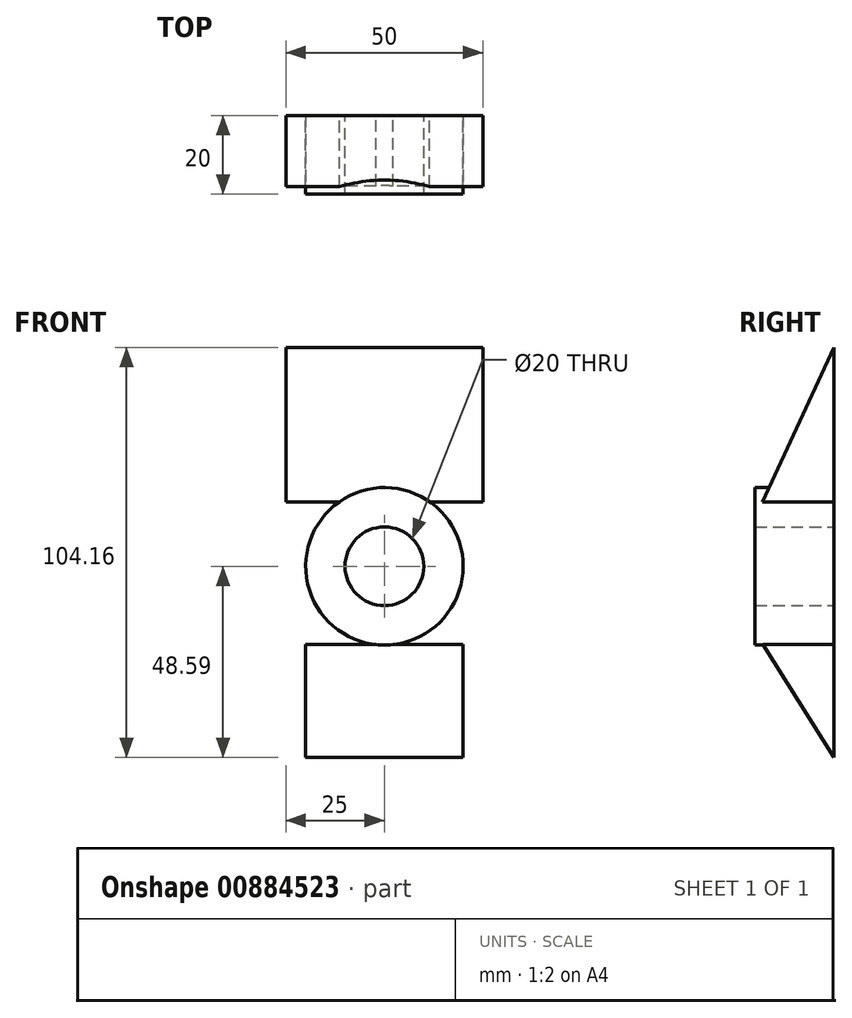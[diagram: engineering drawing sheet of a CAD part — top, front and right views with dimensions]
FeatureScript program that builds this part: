
annotation { "Feature Type Name" : "Feature", "Feature Type Description" : "" }
export const myFeature = defineFeature(function(context is Context, id is Id, definition is map)
    precondition{}
    {
        {
            var Q0;
            Q0=qCreatedBy(makeId("Front.planeOp"),FACE);
            var sketch = newSketch(context, id + "F0", { "sketchPlane" : qUnion([Q0])});
            skCircle(sketch, "E0", {"center": v(0, 0) * mm, "radius": 20 * mm});
            skCircle(sketch, "E1", {"center": v(0, 0) * mm, "radius": 10 * mm});
            skSolve(sketch);
        }
        {
            var Q0;
            Q0=makeQuery(id+"F0.imprint","IMPRINT",FACE,{"disambiguationData":[TD([[makeQuery(id+"F0.imprint","IMPRINT",EDGE,{"derivedFrom":sQuery(id+"F0.wireOp",EDGE,"E0")}),1.0]])]});
            extrude(context, id + "F1", {"entities" : qUnion([Q0]), "depth" : 20 * mm, "offsetDistance" : 25 * mm});
        }
        {
            var Q0;
            Q0=qCreatedBy(makeId("Right.planeOp"),FACE);
            var sketch = newSketch(context, id + "F2", { "sketchPlane" : qUnion([Q0])});
            skLineSegment(sketch, "E2", {"start": v(0, 55.57) * mm, "end": v(0, 16.4) * mm});
            skLineSegment(sketch, "E3", {"start": v(0, 16.4) * mm, "end": v(-18.14, 16.4) * mm});
            skLineSegment(sketch, "E4", {"start": v(-18.14, 16.4) * mm, "end": v(0, 55.57) * mm});
            skSolve(sketch);
        }
        {
            var Q0;
            Q0 = qSketchRegion(id + "F2", true);
            extrude(context, id + "F3", {"entities" : qUnion([Q0]), "operationType" : NewBodyOperationType.ADD, "endBound" : BoundingType.SYMMETRIC, "depth" : 50 * mm, "offsetDistance" : 25 * mm});
        }
        {
            var Q0;
            Q0=qCreatedBy(makeId("Right.planeOp"),FACE);
            var sketch = newSketch(context, id + "F4", { "sketchPlane" : qUnion([Q0])});
            skLineSegment(sketch, "E5", {"start": v(0, -48.59) * mm, "end": v(0, -19.88) * mm});
            skLineSegment(sketch, "E6", {"start": v(0, -19.88) * mm, "end": v(-17.94, -19.88) * mm});
            skLineSegment(sketch, "E7", {"start": v(-17.94, -19.88) * mm, "end": v(0, -48.59) * mm});
            skSolve(sketch);
        }
        {
            var Q0;
            Q0 = qSketchRegion(id + "F4", true);
            extrude(context, id + "F5", {"entities" : qUnion([Q0]), "operationType" : NewBodyOperationType.ADD, "endBound" : BoundingType.SYMMETRIC, "depth" : 40 * mm, "offsetDistance" : 25 * mm});
        }
    });
